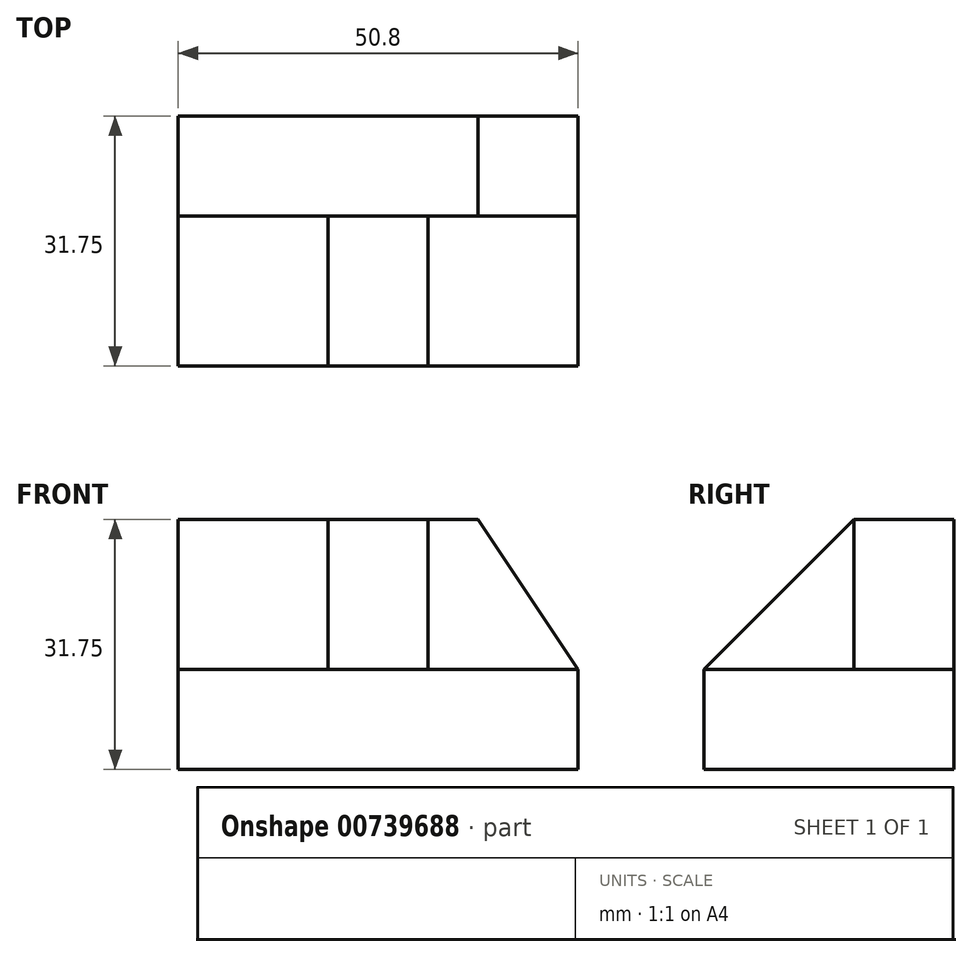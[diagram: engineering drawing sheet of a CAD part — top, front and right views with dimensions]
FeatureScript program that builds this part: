
annotation { "Feature Type Name" : "Feature", "Feature Type Description" : "" }
export const myFeature = defineFeature(function(context is Context, id is Id, definition is map)
    precondition{}
    {
        {
            var Q0;
            Q0=qCreatedBy(makeId("Front.planeOp"),FACE);
            var sketch = newSketch(context, id + "F0", { "sketchPlane" : qUnion([Q0])});
            skLineSegment(sketch, "E0.bottom", {"start": v(0, 0) * mm, "end": v(50.8, 0) * mm});
            skLineSegment(sketch, "E0.top", {"start": v(0, 31.75) * mm, "end": v(50.8, 31.75) * mm});
            skLineSegment(sketch, "E0.left", {"start": v(0, 0) * mm, "end": v(0, 31.75) * mm});
            skLineSegment(sketch, "E0.right", {"start": v(50.8, 0) * mm, "end": v(50.8, 31.75) * mm});
            skSolve(sketch);
        }
        {
            var Q0;
            Q0 = qSketchRegion(id + "F0", true);
            extrude(context, id + "F1", {"entities" : qUnion([Q0]), "depth" : 31.75 * mm, "offsetDistance" : 25.4 * mm});
        }
        {
            var Q0;
            Q0=makeQuery(id+"F1.opExtrude","CAP_FACE",FACE,{"disambiguationData":[OSD([sQuery(id+"F0.wireOp",EDGE,"E0.bottom"),sQuery(id+"F0.wireOp",EDGE,"E0.top"),sQuery(id+"F0.wireOp",EDGE,"E0.left"),sQuery(id+"F0.wireOp",EDGE,"E0.right")])],"isStart":true});
            var sketch = newSketch(context, id + "F2", { "sketchPlane" : qUnion([Q0])});
            skLineSegment(sketch, "E1", {"start": v(-38.1, 31.75) * mm, "end": v(-50.8, 31.75) * mm});
            skLineSegment(sketch, "E2", {"start": v(-50.8, 31.75) * mm, "end": v(-50.8, 12.7) * mm});
            skLineSegment(sketch, "E3", {"start": v(-50.8, 12.7) * mm, "end": v(-38.1, 31.75) * mm});
            skSolve(sketch);
        }
        {
            var Q0;
            Q0 = qSketchRegion(id + "F2", true);
            extrude(context, id + "F3", {"entities" : qUnion([Q0]), "operationType" : NewBodyOperationType.REMOVE, "oppositeDirection" : true, "depth" : 25.4 * mm, "offsetDistance" : 25.4 * mm});
        }
        {
            var Q0;
            Q0=makeQuery(id+"F1.opExtrude","CAP_FACE",FACE,{"disambiguationData":[OSD([sQuery(id+"F0.wireOp",EDGE,"E0.bottom"),sQuery(id+"F0.wireOp",EDGE,"E0.top"),sQuery(id+"F0.wireOp",EDGE,"E0.left"),sQuery(id+"F0.wireOp",EDGE,"E0.right")])],"isStart":false});
            var sketch = newSketch(context, id + "F4", { "sketchPlane" : qUnion([Q0])});
            skLineSegment(sketch, "E4", {"start": v(31.75, 31.75) * mm, "end": v(31.75, 12.7) * mm});
            skLineSegment(sketch, "E5", {"start": v(31.75, 12.7) * mm, "end": v(50.8, 12.7) * mm});
            skLineSegment(sketch, "E6", {"start": v(50.8, 12.7) * mm, "end": v(50.8, 31.75) * mm});
            skLineSegment(sketch, "E7", {"start": v(50.8, 31.75) * mm, "end": v(31.75, 31.75) * mm});
            skSolve(sketch);
        }
        {
            var Q0;
            Q0 = qSketchRegion(id + "F4", true);
            extrude(context, id + "F5", {"entities" : qUnion([Q0]), "operationType" : NewBodyOperationType.REMOVE, "oppositeDirection" : true, "depth" : 19.05 * mm, "offsetDistance" : 25.4 * mm});
        }
        {
            var Q0;
            Q0=makeQuery(id+"F1.opExtrude","SWEPT_FACE",FACE,{"disambiguationData":[OSD([sQuery(id+"F0.wireOp",EDGE,"E0.left")])]});
            var sketch = newSketch(context, id + "F6", { "sketchPlane" : qUnion([Q0])});
            skLineSegment(sketch, "E8", {"start": v(31.75, 12.7) * mm, "end": v(31.75, 31.75) * mm});
            skLineSegment(sketch, "E9", {"start": v(31.75, 31.75) * mm, "end": v(12.7, 31.75) * mm});
            skLineSegment(sketch, "E10", {"start": v(12.7, 31.75) * mm, "end": v(31.75, 12.7) * mm});
            skSolve(sketch);
        }
        {
            var Q0;
            Q0 = qSketchRegion(id + "F6", true);
            extrude(context, id + "F7", {"entities" : qUnion([Q0]), "operationType" : NewBodyOperationType.REMOVE, "oppositeDirection" : true, "depth" : 38.1 * mm, "offsetDistance" : 25.4 * mm});
        }
        {
            var Q0;
            Q0=makeQuery(id+"F1.opExtrude","SWEPT_FACE",FACE,{"disambiguationData":[OSD([sQuery(id+"F0.wireOp",EDGE,"E0.left")])]});
            var sketch = newSketch(context, id + "F8", { "sketchPlane" : qUnion([Q0])});
            skLineSegment(sketch, "E11", {"start": v(12.7, 31.75) * mm, "end": v(12.7, 12.7) * mm});
            skLineSegment(sketch, "E12", {"start": v(12.7, 12.7) * mm, "end": v(31.75, 12.7) * mm});
            skLineSegment(sketch, "E13", {"start": v(31.75, 12.7) * mm, "end": v(12.7, 31.75) * mm});
            skSolve(sketch);
        }
        {
            var Q0;
            Q0 = qSketchRegion(id + "F8", true);
            extrude(context, id + "F9", {"entities" : qUnion([Q0]), "operationType" : NewBodyOperationType.REMOVE, "oppositeDirection" : true, "depth" : 19.05 * mm, "offsetDistance" : 25.4 * mm});
        }
    });
